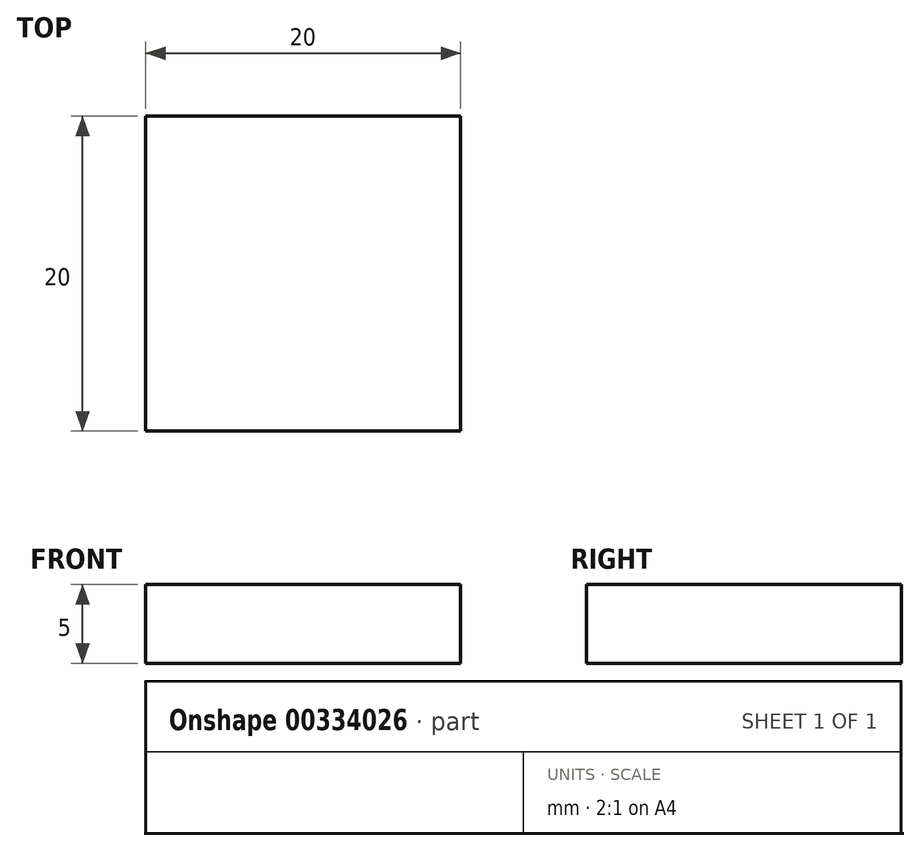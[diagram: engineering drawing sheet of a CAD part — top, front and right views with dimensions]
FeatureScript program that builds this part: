
annotation { "Feature Type Name" : "Feature", "Feature Type Description" : "" }
export const myFeature = defineFeature(function(context is Context, id is Id, definition is map)
    precondition{}
    {
        {
            var Q0;
            Q0=qCreatedBy(makeId("Top.planeOp"),FACE);
            var sketch = newSketch(context, id + "F0", { "sketchPlane" : qUnion([Q0])});
            skLineSegment(sketch, "E0.bottom", {"start": v(-10, 10) * mm, "end": v(10, 10) * mm});
            skLineSegment(sketch, "E0.top", {"start": v(-10, -10) * mm, "end": v(10, -10) * mm});
            skLineSegment(sketch, "E0.left", {"start": v(-10, 10) * mm, "end": v(-10, -10) * mm});
            skLineSegment(sketch, "E0.right", {"start": v(10, 10) * mm, "end": v(10, -10) * mm});
            skSolve(sketch);
        }
        {
            var Q0;
            Q0 = qSketchRegion(id + "F0", true);
            extrude(context, id + "F1", {"entities" : qUnion([Q0]), "depth" : 5 * mm});
        }
    });
